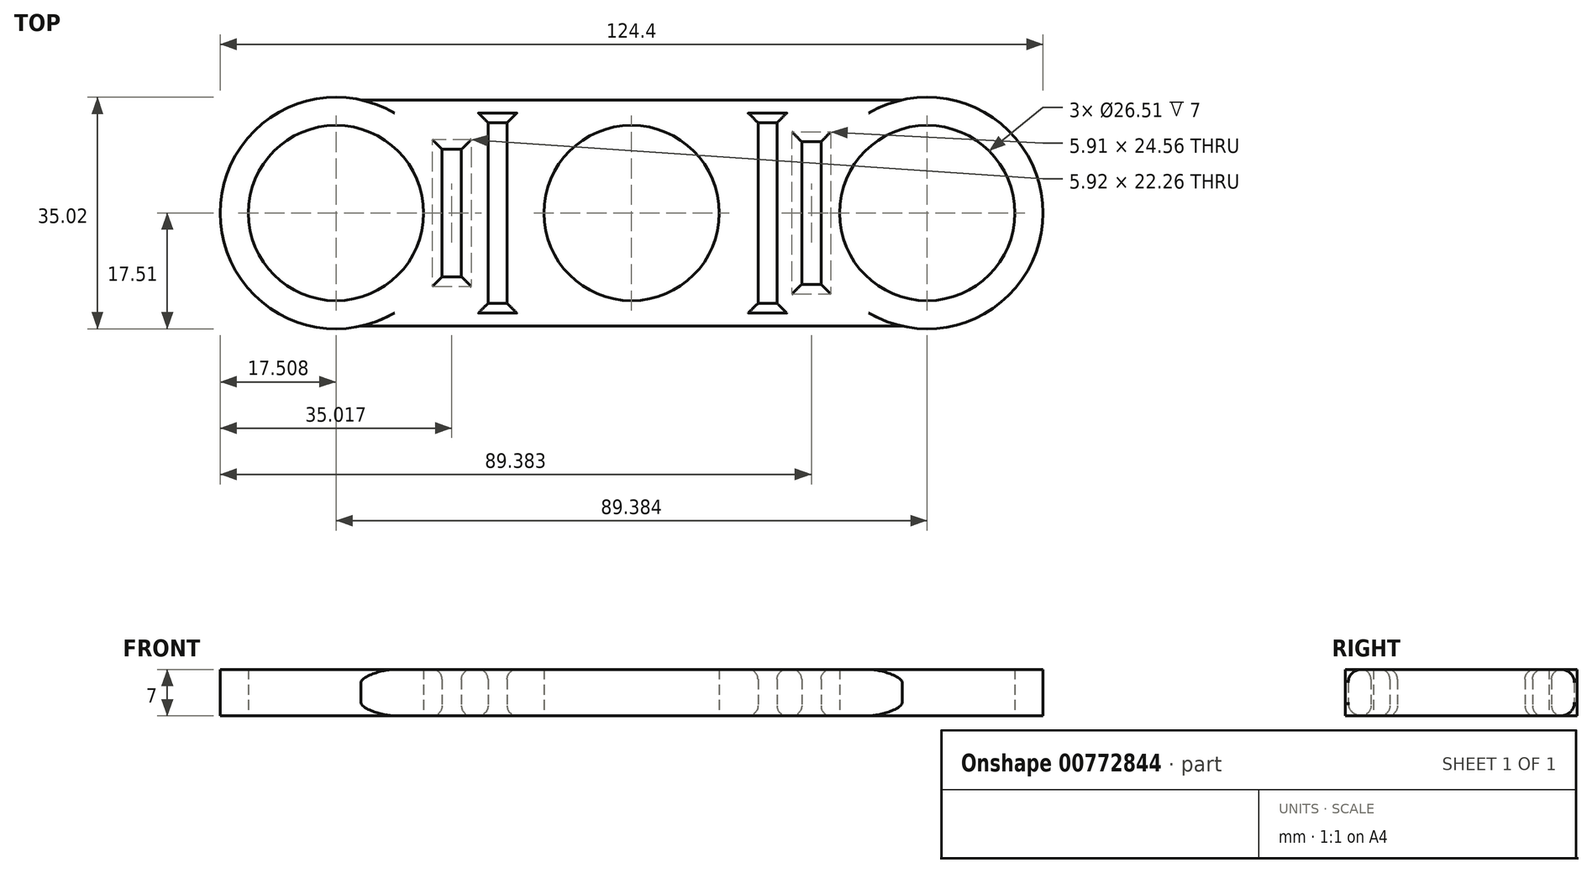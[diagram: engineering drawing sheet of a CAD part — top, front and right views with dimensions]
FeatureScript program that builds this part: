
annotation { "Feature Type Name" : "Feature", "Feature Type Description" : "" }
export const myFeature = defineFeature(function(context is Context, id is Id, definition is map)
    precondition{}
    {
        {
            var Q0;
            Q0=qCreatedBy(makeId("Top.planeOp"),FACE);
            var sketch = newSketch(context, id + "F0", { "sketchPlane" : qUnion([Q0])});
            skLineSegment(sketch, "E0.bottom", {"start": v(44.7, -17.1) * mm, "end": v(-44.7, -17.1) * mm});
            skLineSegment(sketch, "E0.top", {"start": v(44.7, 17.1) * mm, "end": v(-44.7, 17.1) * mm});
            skPoint(sketch, "E0.middle", {"position": v(0, 0) * mm});
            skCircle(sketch, "E1", {"center": v(-44.7, 0) * mm, "radius": 17.5 * mm});
            skCircle(sketch, "E2", {"center": v(44.7, 0) * mm, "radius": 17.5 * mm});
            skCircle(sketch, "E3", {"center": v(0, 0) * mm, "radius": 13.25 * mm});
            skCircle(sketch, "E4", {"center": v(-44.7, 0) * mm, "radius": 13.25 * mm});
            skCircle(sketch, "E5", {"center": v(44.7, 0) * mm, "radius": 13.25 * mm});
            skLineSegment(sketch, "E6.bottom", {"start": v(-18.83, -13.65) * mm, "end": v(-21.7, -13.65) * mm});
            skLineSegment(sketch, "E6.top", {"start": v(-18.83, 13.65) * mm, "end": v(-21.7, 13.65) * mm});
            skLineSegment(sketch, "E6.left", {"start": v(-18.83, -13.65) * mm, "end": v(-18.83, 13.65) * mm});
            skLineSegment(sketch, "E6.right", {"start": v(-21.7, -13.65) * mm, "end": v(-21.7, 13.65) * mm});
            skPoint(sketch, "E6.middle", {"position": v(-20.26, 0) * mm});
            skLineSegment(sketch, "E7.bottom", {"start": v(22, -13.65) * mm, "end": v(19.12, -13.65) * mm});
            skLineSegment(sketch, "E7.top", {"start": v(22, 13.65) * mm, "end": v(19.12, 13.65) * mm});
            skLineSegment(sketch, "E7.left", {"start": v(22, -13.65) * mm, "end": v(22, 13.65) * mm});
            skLineSegment(sketch, "E7.right", {"start": v(19.12, -13.65) * mm, "end": v(19.12, 13.65) * mm});
            skPoint(sketch, "E7.middle", {"position": v(20.55, 0) * mm});
            skLineSegment(sketch, "E8.bottom", {"start": v(-25.72, 9.63) * mm, "end": v(-28.64, 9.63) * mm});
            skLineSegment(sketch, "E8.top", {"start": v(-25.72, -9.63) * mm, "end": v(-28.64, -9.63) * mm});
            skLineSegment(sketch, "E8.left", {"start": v(-25.72, 9.63) * mm, "end": v(-25.72, -9.63) * mm});
            skLineSegment(sketch, "E8.right", {"start": v(-28.64, 9.63) * mm, "end": v(-28.64, -9.63) * mm});
            skPoint(sketch, "E8.middle", {"position": v(-27.18, 0) * mm});
            skLineSegment(sketch, "E9.bottom", {"start": v(25.73, 10.78) * mm, "end": v(28.64, 10.78) * mm});
            skLineSegment(sketch, "E9.top", {"start": v(25.73, -10.78) * mm, "end": v(28.64, -10.78) * mm});
            skLineSegment(sketch, "E9.left", {"start": v(25.73, 10.78) * mm, "end": v(25.73, -10.78) * mm});
            skLineSegment(sketch, "E9.right", {"start": v(28.64, 10.78) * mm, "end": v(28.64, -10.78) * mm});
            skPoint(sketch, "E9.middle", {"position": v(27.18, 0) * mm});
            skSolve(sketch);
        }
        {
            var Q0;
            Q0=makeQuery(id+"F0.imprint","IMPRINT",FACE,{"disambiguationData":[TD([[makeQuery(id+"F0.imprint","IMPRINT",EDGE,{"derivedFrom":sQuery(id+"F0.wireOp",EDGE,"E3")}),-1.0]])]});
            var Q1;
            Q1=makeQuery(id+"F0.imprint","IMPRINT",FACE,{"disambiguationData":[TD([[makeQuery(id+"F0.imprint","IMPRINT",EDGE,{"derivedFrom":sQuery(id+"F0.wireOp",EDGE,"E4")}),-1.0]])]});
            var Q2;
            Q2=makeQuery(id+"F0.imprint","IMPRINT",FACE,{"disambiguationData":[TD([[makeQuery(id+"F0.imprint","IMPRINT",EDGE,{"derivedFrom":sQuery(id+"F0.wireOp",EDGE,"E5")}),-1.0]])]});
            extrude(context, id + "F1", {"entities" : qUnion([Q0, Q1, Q2]), "depth" : 7 * mm, "offsetDistance" : 25 * mm});
        }
        {
            var Q0;
            Q0=makeQuery(id+"F1.opExtrude","CAP_EDGE",EDGE,{"disambiguationData":[OSD([sQuery(id+"F0.wireOp",EDGE,"E0.top")])],"isStart":false});
            var Q1;
            Q1=makeQuery(id+"F1.opExtrude","CAP_EDGE",EDGE,{"disambiguationData":[OSD([sQuery(id+"F0.wireOp",EDGE,"E0.bottom")])],"isStart":false});
            var Q2;
            Q2=makeQuery(id+"F1.opExtrude","CAP_EDGE",EDGE,{"disambiguationData":[OSD([sQuery(id+"F0.wireOp",EDGE,"E0.bottom")])],"isStart":true});
            var Q3;
            Q3=makeQuery(id+"F1.opExtrude","CAP_EDGE",EDGE,{"disambiguationData":[OSD([sQuery(id+"F0.wireOp",EDGE,"E0.top")])],"isStart":true});
            fillet(context, id + "F2", {"entities" : qUnion([Q0, Q1, Q2, Q3]), "radius" : 2 * mm, "tangentPropagation" : true, "allowEdgeOverflow" : false});
        }
        {
            var Q0;
            Q0=makeQuery(id+"F1.opExtrude","CAP_EDGE",EDGE,{"disambiguationData":[OSD([sQuery(id+"F0.wireOp",EDGE,"E8.right")])],"isStart":false});
            var Q1;
            Q1=makeQuery(id+"F1.opExtrude","CAP_EDGE",EDGE,{"disambiguationData":[OSD([sQuery(id+"F0.wireOp",EDGE,"E8.bottom")])],"isStart":false});
            var Q2;
            Q2=makeQuery(id+"F1.opExtrude","CAP_EDGE",EDGE,{"disambiguationData":[OSD([sQuery(id+"F0.wireOp",EDGE,"E8.left")])],"isStart":false});
            var Q3;
            Q3=makeQuery(id+"F1.opExtrude","CAP_EDGE",EDGE,{"disambiguationData":[OSD([sQuery(id+"F0.wireOp",EDGE,"E8.top")])],"isStart":false});
            var Q4;
            Q4=makeQuery(id+"F1.opExtrude","CAP_EDGE",EDGE,{"disambiguationData":[OSD([sQuery(id+"F0.wireOp",EDGE,"E6.right")])],"isStart":false});
            var Q5;
            Q5=makeQuery(id+"F1.opExtrude","CAP_EDGE",EDGE,{"disambiguationData":[OSD([sQuery(id+"F0.wireOp",EDGE,"E6.bottom")])],"isStart":false});
            var Q6;
            Q6=makeQuery(id+"F1.opExtrude","CAP_EDGE",EDGE,{"disambiguationData":[OSD([sQuery(id+"F0.wireOp",EDGE,"E6.left")])],"isStart":false});
            var Q7;
            Q7=makeQuery(id+"F1.opExtrude","CAP_EDGE",EDGE,{"disambiguationData":[OSD([sQuery(id+"F0.wireOp",EDGE,"E6.top")])],"isStart":false});
            var Q8;
            Q8=makeQuery(id+"F1.opExtrude","CAP_EDGE",EDGE,{"disambiguationData":[OSD([sQuery(id+"F0.wireOp",EDGE,"E7.right")])],"isStart":false});
            var Q9;
            Q9=makeQuery(id+"F1.opExtrude","CAP_EDGE",EDGE,{"disambiguationData":[OSD([sQuery(id+"F0.wireOp",EDGE,"E7.left")])],"isStart":false});
            var Q10;
            Q10=makeQuery(id+"F1.opExtrude","CAP_EDGE",EDGE,{"disambiguationData":[OSD([sQuery(id+"F0.wireOp",EDGE,"E7.bottom")])],"isStart":false});
            var Q11;
            Q11=makeQuery(id+"F1.opExtrude","CAP_EDGE",EDGE,{"disambiguationData":[OSD([sQuery(id+"F0.wireOp",EDGE,"E7.top")])],"isStart":false});
            var Q12;
            Q12=makeQuery(id+"F1.opExtrude","CAP_EDGE",EDGE,{"disambiguationData":[OSD([sQuery(id+"F0.wireOp",EDGE,"E9.left")])],"isStart":false});
            var Q13;
            Q13=makeQuery(id+"F1.opExtrude","CAP_EDGE",EDGE,{"disambiguationData":[OSD([sQuery(id+"F0.wireOp",EDGE,"E9.bottom")])],"isStart":false});
            var Q14;
            Q14=makeQuery(id+"F1.opExtrude","CAP_EDGE",EDGE,{"disambiguationData":[OSD([sQuery(id+"F0.wireOp",EDGE,"E9.right")])],"isStart":false});
            var Q15;
            Q15=makeQuery(id+"F1.opExtrude","CAP_EDGE",EDGE,{"disambiguationData":[OSD([sQuery(id+"F0.wireOp",EDGE,"E9.top")])],"isStart":false});
            var Q16;
            Q16=makeQuery(id+"F1.opExtrude","CAP_EDGE",EDGE,{"disambiguationData":[OSD([sQuery(id+"F0.wireOp",EDGE,"E8.top")])],"isStart":true});
            var Q17;
            Q17=makeQuery(id+"F1.opExtrude","CAP_EDGE",EDGE,{"disambiguationData":[OSD([sQuery(id+"F0.wireOp",EDGE,"E8.right")])],"isStart":true});
            var Q18;
            Q18=makeQuery(id+"F1.opExtrude","CAP_EDGE",EDGE,{"disambiguationData":[OSD([sQuery(id+"F0.wireOp",EDGE,"E8.left")])],"isStart":true});
            var Q19;
            Q19=makeQuery(id+"F1.opExtrude","CAP_EDGE",EDGE,{"disambiguationData":[OSD([sQuery(id+"F0.wireOp",EDGE,"E8.bottom")])],"isStart":true});
            var Q20;
            Q20=makeQuery(id+"F1.opExtrude","CAP_EDGE",EDGE,{"disambiguationData":[OSD([sQuery(id+"F0.wireOp",EDGE,"E6.top")])],"isStart":true});
            var Q21;
            Q21=makeQuery(id+"F1.opExtrude","CAP_EDGE",EDGE,{"disambiguationData":[OSD([sQuery(id+"F0.wireOp",EDGE,"E6.right")])],"isStart":true});
            var Q22;
            Q22=makeQuery(id+"F1.opExtrude","CAP_EDGE",EDGE,{"disambiguationData":[OSD([sQuery(id+"F0.wireOp",EDGE,"E6.left")])],"isStart":true});
            var Q23;
            Q23=makeQuery(id+"F1.opExtrude","CAP_EDGE",EDGE,{"disambiguationData":[OSD([sQuery(id+"F0.wireOp",EDGE,"E6.bottom")])],"isStart":true});
            var Q24;
            Q24=makeQuery(id+"F1.opExtrude","CAP_EDGE",EDGE,{"disambiguationData":[OSD([sQuery(id+"F0.wireOp",EDGE,"E7.right")])],"isStart":true});
            var Q25;
            Q25=makeQuery(id+"F1.opExtrude","CAP_EDGE",EDGE,{"disambiguationData":[OSD([sQuery(id+"F0.wireOp",EDGE,"E7.left")])],"isStart":true});
            var Q26;
            Q26=makeQuery(id+"F1.opExtrude","CAP_EDGE",EDGE,{"disambiguationData":[OSD([sQuery(id+"F0.wireOp",EDGE,"E7.top")])],"isStart":true});
            var Q27;
            Q27=makeQuery(id+"F1.opExtrude","CAP_EDGE",EDGE,{"disambiguationData":[OSD([sQuery(id+"F0.wireOp",EDGE,"E7.bottom")])],"isStart":true});
            var Q28;
            Q28=makeQuery(id+"F1.opExtrude","CAP_EDGE",EDGE,{"disambiguationData":[OSD([sQuery(id+"F0.wireOp",EDGE,"E9.top")])],"isStart":true});
            var Q29;
            Q29=makeQuery(id+"F1.opExtrude","CAP_EDGE",EDGE,{"disambiguationData":[OSD([sQuery(id+"F0.wireOp",EDGE,"E9.right")])],"isStart":true});
            var Q30;
            Q30=makeQuery(id+"F1.opExtrude","CAP_EDGE",EDGE,{"disambiguationData":[OSD([sQuery(id+"F0.wireOp",EDGE,"E9.left")])],"isStart":true});
            var Q31;
            Q31=makeQuery(id+"F1.opExtrude","CAP_EDGE",EDGE,{"disambiguationData":[OSD([sQuery(id+"F0.wireOp",EDGE,"E9.bottom")])],"isStart":true});
            fillet(context, id + "F3", {"entities" : qUnion([Q0, Q1, Q2, Q3, Q4, Q5, Q6, Q7, Q8, Q9, Q10, Q11, Q12, Q13, Q14, Q15, Q16, Q17, Q18, Q19, Q20, Q21, Q22, Q23, Q24, Q25, Q26, Q27, Q28, Q29, Q30, Q31]), "radius" : 1.5 * mm, "tangentPropagation" : true, "allowEdgeOverflow" : false});
        }
    });
